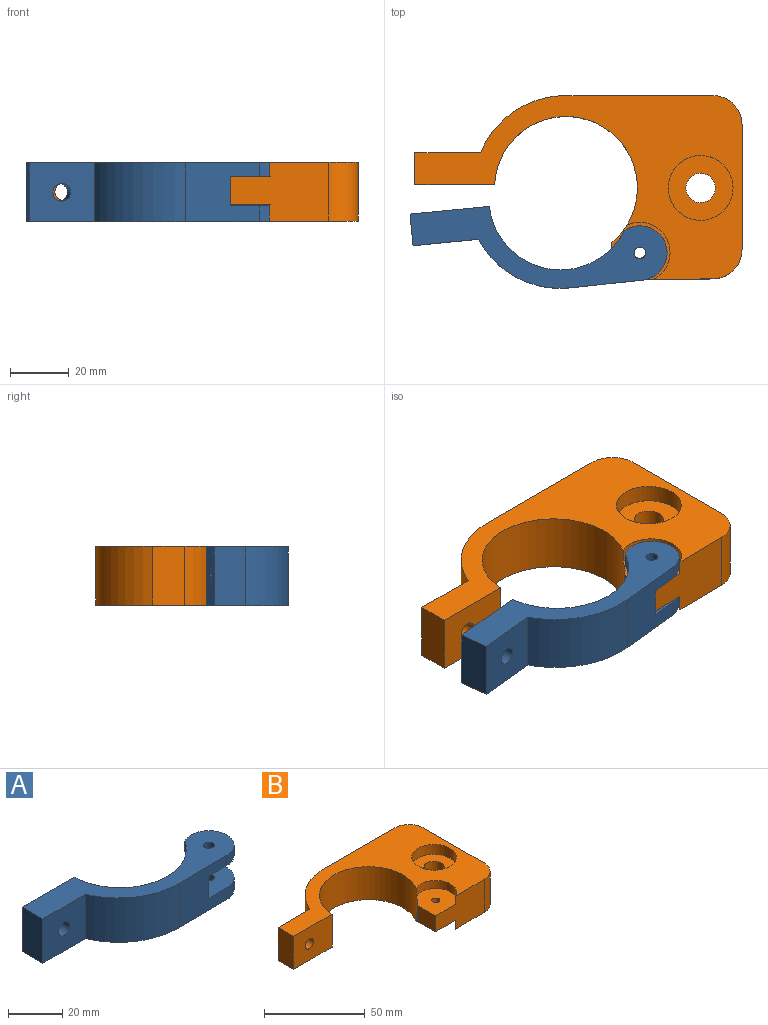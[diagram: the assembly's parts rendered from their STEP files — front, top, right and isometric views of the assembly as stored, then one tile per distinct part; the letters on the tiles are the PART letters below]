
ASSEMBLY  parts=2 mates=1
PART A: 16 faces, bbox 86x30.3x20 mm
  f0: plane 25.08x20mm, normal (0.01,-1,0), area 403.1mm2, adj f2,f6,f7,f8,f10,f12,f13,f14
  f1: cylinder r=2mm len=4.65mm, axis (0,0,1), area 58.4mm2, adj f7,f12
  f2: cylinder r=9.27mm len=18.54mm, axis (0,0,1), area 156mm2, adj f0,f3,f7,f12
  f3: cylinder r=24.46mm len=45.12mm, axis (0,0,1), area 1170.9mm2, adj f2,f7,f8,f10,f11,f12,f13,f14
  f4: plane 20x10.8mm, normal (-1,0,0), area 216mm2, adj f5,f7,f8,f11
  f5: plane 22.38x20mm, normal (0,-1,0), area 419.2mm2, adj f4,f6,f7,f8,f15
  f6: cylinder r=31.5mm len=29.44mm, axis (0,0,-1), area 749.7mm2, adj f0,f5,f7,f8
  f7: plane 85.98x30.3mm, normal (0,0,1), area 911.8mm2, adj f0,f1,f2,f3,f4,f5,f6,f11
  f8: plane 85.98x30.3mm, normal (0,0,-1), area 911.8mm2, adj f0,f3,f4,f5,f6,f9,f10,f11
  f9: cylinder r=2mm len=5.35mm, axis (0,0,1), area 67.3mm2, adj f8,f14
  f10: cylinder r=9.27mm len=18.54mm, axis (0,0,1), area 179.8mm2, adj f0,f3,f8,f14
  f11: plane 27.15x20mm, normal (0,1,0), area 514.7mm2, adj f3,f4,f7,f8,f15
  f12: plane 19.05x18.64mm, normal (0,0,-1), area 278.3mm2, adj f0,f1,f2,f3,f13
  f13: plane 11.54x10mm, normal (1,0.01,0), area 115.4mm2, adj f0,f3,f12,f14
  f14: plane 19.05x18.64mm, normal (0,0,1), area 278.3mm2, adj f0,f3,f9,f10,f13
  f15: cylinder r=3mm len=10.8mm, axis (0,-1,0), area 203.6mm2, adj f5,f11
PART B: 29 faces, bbox 111.5x62.8x20 mm
  f0: plane 22.38x20mm, normal (0,1,0), area 361.7mm2, adj f9,f10,f11,f13,f23,f24,f25,f26
  f1: cylinder r=3mm len=6mm, axis (0,-1,0), area 109.3mm2, adj f15,f22
  f2: cylinder r=5mm len=14mm, axis (0,0,-1), area 439.8mm2, adj f10,f21
  f3: cylinder r=24.35mm len=48.67mm, axis (0,0,-1), area 1850mm2, adj f4,f10,f11,f14,f15,f16,f17,f18
  f4: cylinder r=10.27mm len=19.5mm, axis (0,0,1), area 178.3mm2, adj f3,f10,f12,f16
  f5: cylinder r=10mm len=20mm, axis (0,0,-1), area 312.2mm2, adj f6,f10,f11,f12
  f6: plane 42.5x20mm, normal (1,0,0), area 850mm2, adj f5,f7,f10,f11
  f7: cylinder r=10mm len=20mm, axis (0,0,-1), area 314.2mm2, adj f6,f8,f10,f11
  f8: plane 50x20mm, normal (0,1,0), area 1000mm2, adj f7,f9,f10,f11
  f9: cylinder r=31.5mm len=29.12mm, axis (0,0,-1), area 743.4mm2, adj f0,f8,f10,f11
  f10: plane 111.5x62.7mm, normal (0,0,-1), area 2774.8mm2, adj f0,f2,f3,f4,f5,f6,f7,f8
  f11: plane 111.5x62.7mm, normal (0,0,1), area 2469.8mm2, adj f0,f3,f5,f6,f7,f8,f9,f12
  f12: plane 34.37x20mm, normal (0.01,-1,0), area 542.3mm2, adj f4,f5,f10,f11,f14,f16,f17,f18
  f13: plane 20x10.8mm, normal (-1,0,0), area 216mm2, adj f0,f10,f11,f15
  f14: cylinder r=10.27mm len=19.5mm, axis (0,0,1), area 155.6mm2, adj f3,f11,f12,f17
  f15: plane 27.18x20mm, normal (0,-1,0), area 515.3mm2, adj f1,f3,f10,f11,f13
  f16: plane 19.88x19.64mm, normal (0,0,-1), area 313.7mm2, adj f3,f4,f12,f18,f19
  f17: plane 19.88x19.64mm, normal (0,0,1), area 313.7mm2, adj f3,f12,f14,f18,f19
  f18: plane 12.65x9.63mm, normal (-1,-0.01,0), area 121.8mm2, adj f3,f12,f16,f17
  f19: cylinder r=2mm len=9.63mm, axis (0,0,1), area 121mm2, adj f16,f17
  f20: cylinder r=11.05mm len=22.1mm, axis (0,0,1), area 416.6mm2, adj f11,f21
  f21: plane 22.1x22.1mm, normal (0,0,1), area 305.1mm2, adj f2,f20
  f22: plane 11.4x10.6mm, normal (0,1,0), area 57.5mm2, adj f1,f23,f24,f25,f26,f27,f28
  f23: plane 5.7x5mm, normal (0.13,0,0.99), area 28.7mm2, adj f0,f22,f24,f28
  f24: plane 5.3x5mm, normal (0.92,0,0.39), area 28.7mm2, adj f0,f22,f23,f25
  f25: plane 5x4.57mm, normal (0.8,0,-0.61), area 28.7mm2, adj f0,f22,f24,f26
  f26: plane 5.7x5mm, normal (-0.13,0,-0.99), area 28.7mm2, adj f0,f22,f25,f27
  f27: plane 5.3x5mm, normal (-0.92,0,-0.39), area 28.7mm2, adj f0,f22,f26,f28
  f28: plane 5x4.57mm, normal (-0.8,0,0.61), area 28.7mm2, adj f0,f22,f23,f27
PLACE A rot(axis=(0,0,1),5.5deg) t=(-2.02,-2.74,-0.19)mm
PLACE B at identity fixed
MATE revolute B.f17 <-> A.f1  axis (0,0,1) through (25.19,-22.18,262.17)mm
